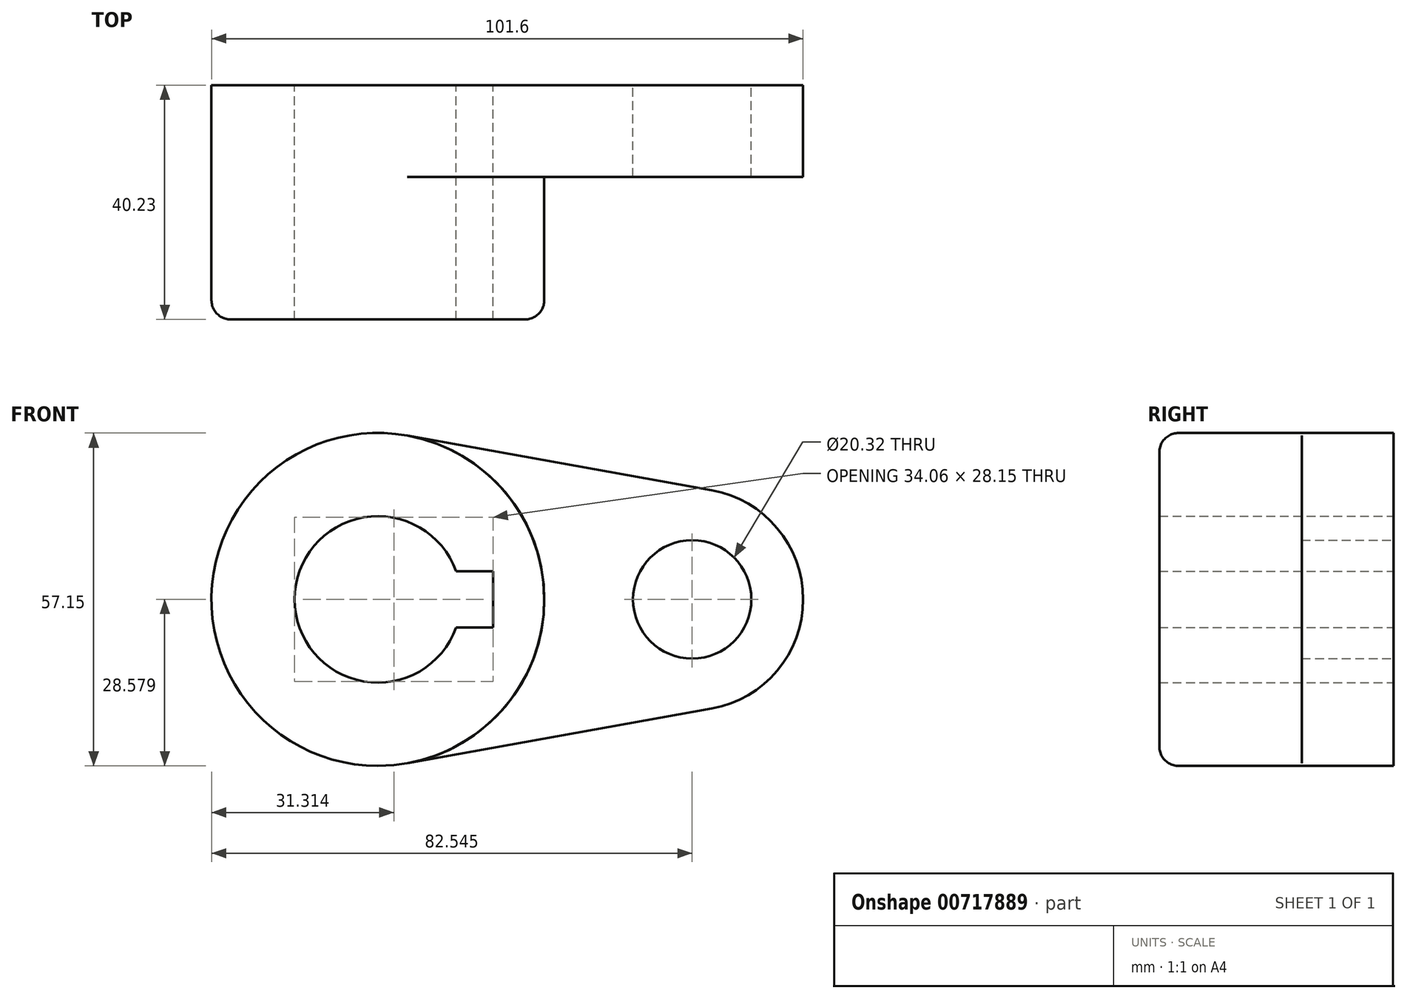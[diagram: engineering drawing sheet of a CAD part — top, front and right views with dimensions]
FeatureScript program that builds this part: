
annotation { "Feature Type Name" : "Feature", "Feature Type Description" : "" }
export const myFeature = defineFeature(function(context is Context, id is Id, definition is map)
    precondition{}
    {
        {
            var Q0;
            Q0=qCreatedBy(makeId("Front.planeOp"),FACE);
            var sketch = newSketch(context, id + "F0", { "sketchPlane" : qUnion([Q0])});
            skCircle(sketch, "E0", {"center": v(-52.9, 24.66) * mm, "radius": 28.58 * mm});
            skArc(sketch, "E1", {"start": v(-39.46, 29.49) * mm, "mid": v(-67.2, 24.66) * mm, "end": v(-39.46, 19.83) * mm});
            skCircle(sketch, "E2", {"center": v(1.07, 24.66) * mm, "radius": 10.16 * mm});
            skArc(sketch, "E3", {"start": v(4.43, 5.9) * mm, "mid": v(20.12, 24.66) * mm, "end": v(4.43, 43.41) * mm});
            skLineSegment(sketch, "E4", {"start": v(-47.87, -3.47) * mm, "end": v(4.43, 5.9) * mm});
            skLineSegment(sketch, "E5", {"start": v(-47.87, 52.79) * mm, "end": v(4.43, 43.41) * mm});
            skLineSegment(sketch, "E6", {"start": v(-52.9, 24.66) * mm, "end": v(1.07, 24.66) * mm, "construction": true});
            skLineSegment(sketch, "E7", {"start": v(-33.14, 24.66) * mm, "end": v(-33.14, 29.49) * mm});
            skLineSegment(sketch, "E8", {"start": v(-33.14, 29.49) * mm, "end": v(-39.46, 29.49) * mm});
            skLineSegment(sketch, "E9", {"start": v(-33.14, 24.66) * mm, "end": v(-33.14, 19.83) * mm});
            skLineSegment(sketch, "E10", {"start": v(-33.14, 19.83) * mm, "end": v(-39.46, 19.83) * mm});
            skSolve(sketch);
        }
        {
            var Q0;
            Q0=makeQuery(id+"F0.imprint","IMPRINT",FACE,{"disambiguationData":[TD([[makeQuery(id+"F0.imprint","IMPRINT",EDGE,{"derivedFrom":sQuery(id+"F0.wireOp",EDGE,"E2")}),-1.0]])]});
            extrude(context, id + "F1", {"entities" : qUnion([Q0]), "depth" : 15.77 * mm, "offsetDistance" : 25.4 * mm});
        }
        {
            var Q0;
            Q0=makeQuery(id+"F0.imprint","IMPRINT",FACE,{"disambiguationData":[TD([[makeQuery(id+"F0.imprint","IMPRINT",EDGE,{"derivedFrom":sQuery(id+"F0.wireOp",EDGE,"E1")}),-1.0]])]});
            extrude(context, id + "F2", {"entities" : qUnion([Q0]), "operationType" : NewBodyOperationType.ADD, "depth" : 40.23 * mm, "offsetDistance" : 25.4 * mm});
        }
        {
            var Q0;
            Q0=makeQuery(id+"F2.opExtrude","CAP_EDGE",EDGE,{"disambiguationData":[OSD([sQuery(id+"F0.wireOp",EDGE,"E0")])],"isStart":false});
            fillet(context, id + "F3", {"entities" : qUnion([Q0]), "radius" : 3.3 * mm, "tangentPropagation" : true, "allowEdgeOverflow" : false});
        }
    });
